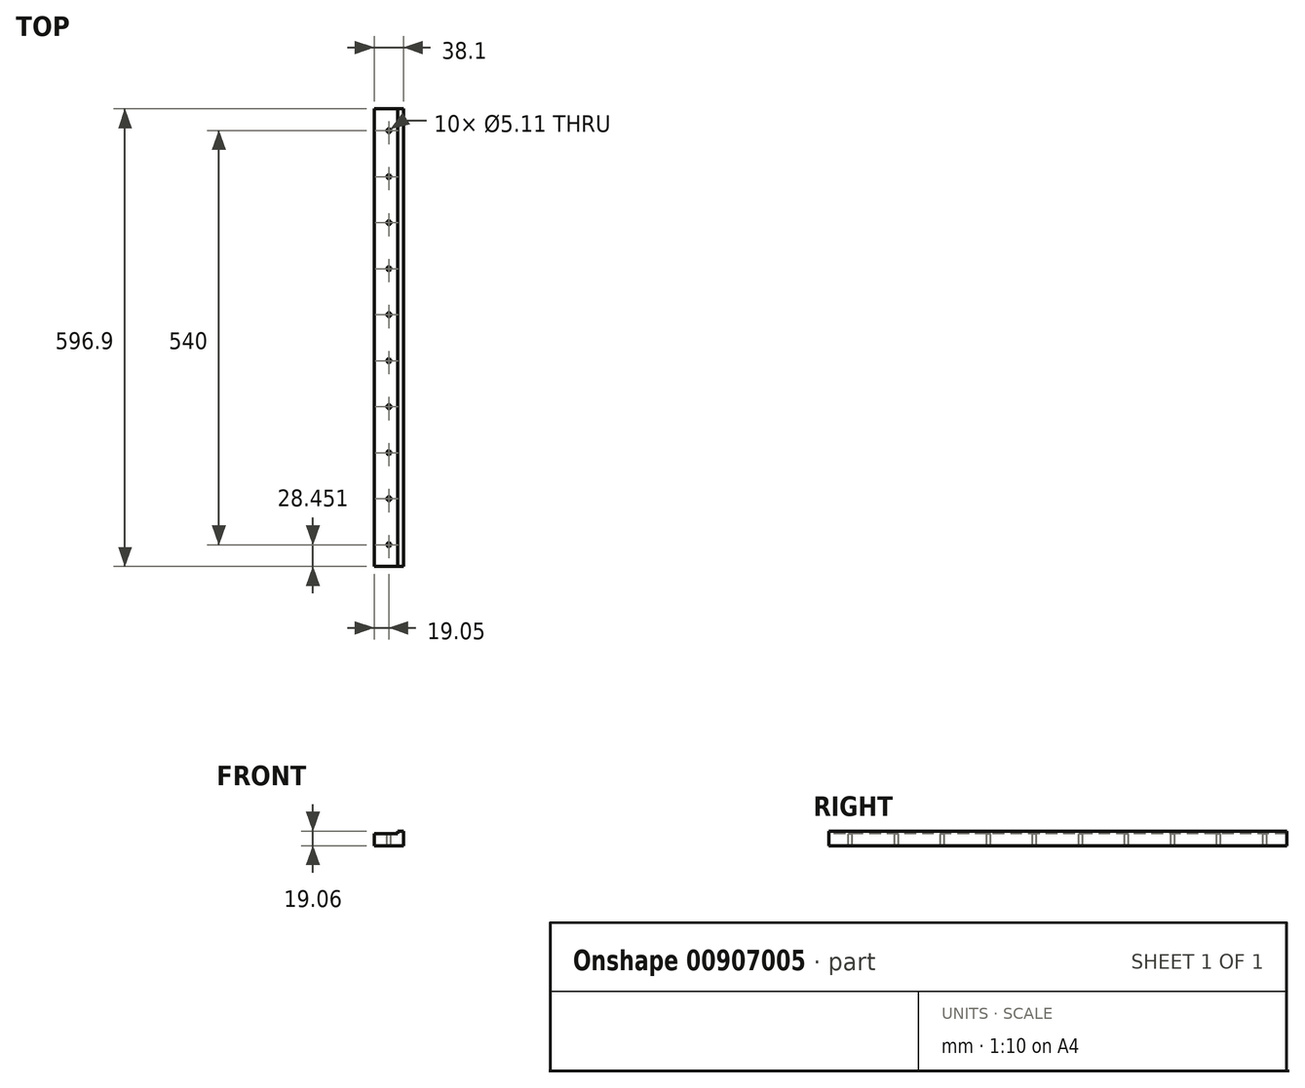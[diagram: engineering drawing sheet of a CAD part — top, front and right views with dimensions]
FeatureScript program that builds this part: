
annotation { "Feature Type Name" : "Feature", "Feature Type Description" : "" }
export const myFeature = defineFeature(function(context is Context, id is Id, definition is map)
    precondition{}
    {
        {
            var Q0;
            Q0=qCreatedBy(makeId("Front.planeOp"),FACE);
            var sketch = newSketch(context, id + "F0", { "sketchPlane" : qUnion([Q0])});
            skLineSegment(sketch, "E0.bottom", {"start": v(19.05, 9.52) * mm, "end": v(-19.05, 9.52) * mm});
            skLineSegment(sketch, "E0.top", {"start": v(19.05, -9.53) * mm, "end": v(-19.05, -9.53) * mm});
            skLineSegment(sketch, "E0.left", {"start": v(19.05, 9.52) * mm, "end": v(19.05, -9.53) * mm});
            skLineSegment(sketch, "E0.right", {"start": v(-19.05, 9.52) * mm, "end": v(-19.05, -9.53) * mm});
            skPoint(sketch, "E0.middle", {"position": v(0, 0) * mm});
            skSolve(sketch);
        }
        {
            var Q0;
            Q0=makeQuery(id+"F0.imprint","IMPRINT",FACE,{"disambiguationData":[TD([[makeQuery(id+"F0.imprint","IMPRINT",EDGE,{"derivedFrom":sQuery(id+"F0.wireOp",EDGE,"E0.bottom")}),1.0]])]});
            extrude(context, id + "F1", {"entities" : qUnion([Q0]), "depth" : 596.9 * mm, "offsetDistance" : 25.4 * mm});
        }
        {
            var Q0;
            Q0=makeQuery(id+"F1.opExtrude","CAP_FACE",FACE,{"disambiguationData":[OSD([sQuery(id+"F0.wireOp",EDGE,"E0.bottom"),sQuery(id+"F0.wireOp",EDGE,"E0.top"),sQuery(id+"F0.wireOp",EDGE,"E0.left"),sQuery(id+"F0.wireOp",EDGE,"E0.right")])],"isStart":false});
            var sketch = newSketch(context, id + "F2", { "sketchPlane" : qUnion([Q0])});
            skLineSegment(sketch, "E1.bottom", {"start": v(-19.05, 9.52) * mm, "end": v(11.5, 9.52) * mm});
            skLineSegment(sketch, "E1.top", {"start": v(-19.05, 6.35) * mm, "end": v(11.5, 6.35) * mm});
            skLineSegment(sketch, "E1.left", {"start": v(-19.05, 9.52) * mm, "end": v(-19.05, 6.35) * mm});
            skLineSegment(sketch, "E1.right", {"start": v(11.5, 9.52) * mm, "end": v(11.5, 6.35) * mm});
            skSolve(sketch);
        }
        {
            var Q0;
            Q0=makeQuery(id+"F2.imprint","IMPRINT",FACE,{"disambiguationData":[TD([[makeQuery(id+"F2.imprint","IMPRINT",EDGE,{"derivedFrom":sQuery(id+"F2.wireOp",EDGE,"E1.bottom")}),1.0]])]});
            extrude(context, id + "F3", {"entities" : qUnion([Q0]), "operationType" : NewBodyOperationType.REMOVE, "endBound" : BoundingType.THROUGH_ALL, "oppositeDirection" : true, "depth" : 25.4 * mm, "offsetDistance" : 25.4 * mm});
        }
        {
            var Q0;
            Q0=makeQuery(id+"F3.boolean.opBoolean","COPY",FACE,{"derivedFrom":makeQuery(id+"F3.opExtrude","SWEPT_FACE",FACE,{"disambiguationData":[OSD([sQuery(id+"F2.wireOp",EDGE,"E1.top")])]})});
            var sketch = newSketch(context, id + "F4", { "sketchPlane" : qUnion([Q0])});
            skPoint(sketch, "E2", {"position": v(0, -568.45) * mm});
            skPoint(sketch, "E3.0.1.0", {"position": v(0, -508.45) * mm});
            skPoint(sketch, "E3.0.2.0", {"position": v(0, -448.45) * mm});
            skPoint(sketch, "E3.0.3.0", {"position": v(0, -388.45) * mm});
            skPoint(sketch, "E3.0.4.0", {"position": v(0, -328.45) * mm});
            skPoint(sketch, "E3.0.5.0", {"position": v(0, -268.45) * mm});
            skPoint(sketch, "E3.0.6.0", {"position": v(0, -208.45) * mm});
            skPoint(sketch, "E3.0.7.0", {"position": v(0, -148.45) * mm});
            skPoint(sketch, "E3.0.8.0", {"position": v(0, -88.45) * mm});
            skPoint(sketch, "E3.0.9.0", {"position": v(0, -28.45) * mm});
            skLineSegment(sketch, "E3.direction1", {"start": v(0, -568.45) * mm, "end": v(25.4, -568.45) * mm, "construction": true});
            skLineSegment(sketch, "E3.direction2", {"start": v(0, -568.45) * mm, "end": v(0, -508.45) * mm, "construction": true});
            skSolve(sketch);
        }
        {
            var Q0;
            Q0=sQuery(id+"F4.wireOp",VERTEX,"E2");
            var Q1;
            Q1=sQuery(id+"F4.wireOp",VERTEX,"E3.0.1.0");
            var Q2;
            Q2=sQuery(id+"F4.wireOp",VERTEX,"E3.0.2.0");
            var Q3;
            Q3=sQuery(id+"F4.wireOp",VERTEX,"E3.0.3.0");
            var Q4;
            Q4=sQuery(id+"F4.wireOp",VERTEX,"E3.0.4.0");
            var Q5;
            Q5=sQuery(id+"F4.wireOp",VERTEX,"E3.0.5.0");
            var Q6;
            Q6=sQuery(id+"F4.wireOp",VERTEX,"E3.0.6.0");
            var Q7;
            Q7=sQuery(id+"F4.wireOp",VERTEX,"E3.0.7.0");
            var Q8;
            Q8=sQuery(id+"F4.wireOp",VERTEX,"E3.0.8.0");
            var Q9;
            Q9=sQuery(id+"F4.wireOp",VERTEX,"E3.0.9.0");
            var Q10;
            Q10=makeQuery(id+"F1.opExtrude","SWEPT_BODY",BODY,{"disambiguationData":[OSD([sQuery(id+"F0.wireOp",EDGE,"E0.bottom"),sQuery(id+"F0.wireOp",EDGE,"E0.top"),sQuery(id+"F0.wireOp",EDGE,"E0.left"),sQuery(id+"F0.wireOp",EDGE,"E0.right")])]});
            hole(context, id + "F5", {"style" : HoleStyle.SIMPLE, "endStyle" : HoleEndStyle.BLIND, "standardTappedOrClearance" : lookupTablePath({ "standard" : "ANSI", "engagement" : "75%", "pitch" : "20 tpi", "size" : "1/4", "type" : "Tapped" }), "standardBlindInLast" : lookupTablePath({ "standard" : "ANSI", "fit" : "Free", "engagement" : "75%", "pitch" : "20 tpi", "size" : "1/4", "type" : "Clearance & tapped" }), "holeDiameter" : 5.1 * mm, "majorDiameter" : 6.35 * mm, "showTappedDepth" : true, "holeDepth" : 16.51 * mm, "isTappedThrough" : true, "tappedDepth" : 12.7 * mm, "tapClearance" : 3, "locations" : qUnion([Q0, Q1, Q2, Q3, Q4, Q5, Q6, Q7, Q8, Q9]), "scope" : qUnion([Q10])});
        }
    });
